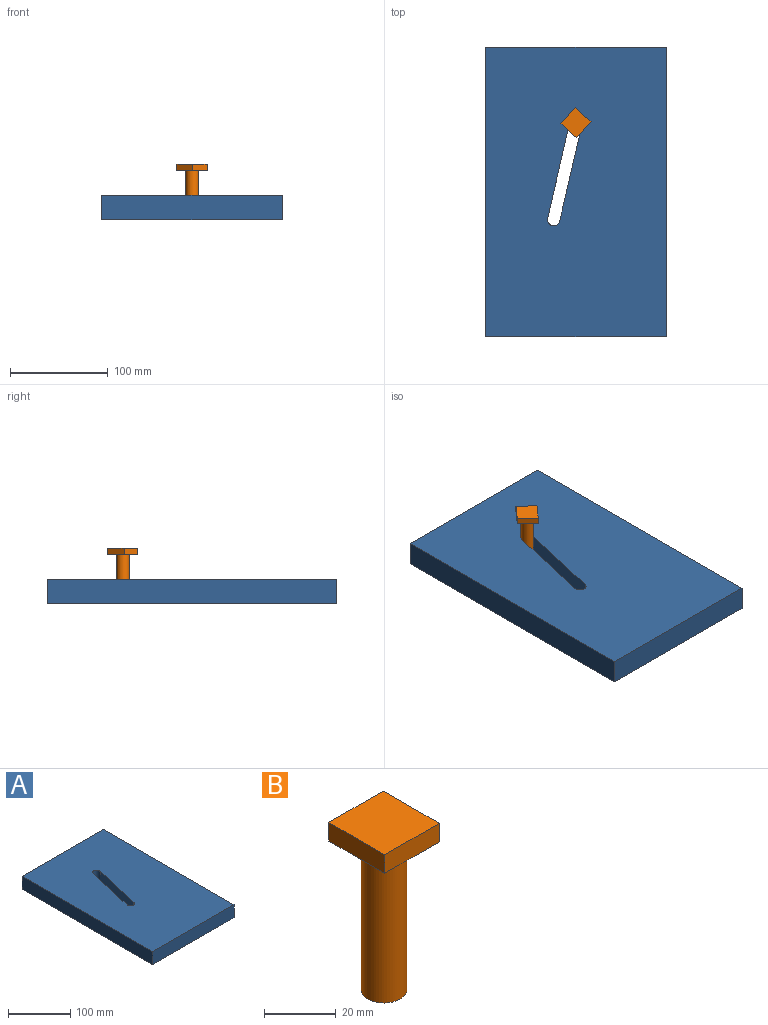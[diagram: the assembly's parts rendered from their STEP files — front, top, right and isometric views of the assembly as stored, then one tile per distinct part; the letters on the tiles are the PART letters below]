
ASSEMBLY  parts=2 mates=1
PART A: 10 faces, bbox 184.2x296x25.4 mm
  f0: plane 99.01x25.4mm, normal (-0.97,0.22,0), area 2580.6mm2, adj f1,f7,f8,f9
  f1: cylinder r=6.35mm len=25.4mm, axis (0,0,-1), area 506.7mm2, adj f0,f2,f8,f9
  f2: plane 99.01x25.4mm, normal (0.97,-0.22,0), area 2580.6mm2, adj f1,f7,f8,f9
  f3: plane 184.15x25.4mm, normal (0,1,0), area 4677.4mm2, adj f4,f6,f8,f9
  f4: plane 295.96x25.4mm, normal (-1,0,0), area 7517.4mm2, adj f3,f5,f8,f9
  f5: plane 184.15x25.4mm, normal (0,-1,0), area 4677.4mm2, adj f4,f6,f8,f9
  f6: plane 295.96x25.4mm, normal (1,0,0), area 7517.4mm2, adj f3,f5,f8,f9
  f7: cylinder r=6.35mm len=25.4mm, axis (0,0,-1), area 506.7mm2, adj f0,f2,f8,f9
  f8: plane 295.96x184.15mm, normal (0,0,1), area 53084.3mm2, adj f0,f1,f2,f3,f4,f5,f6,f7
  f9: plane 295.96x184.15mm, normal (0,0,-1), area 53084.3mm2, adj f0,f1,f2,f3,f4,f5,f6,f7
PART B: 8 faces, bbox 21.5x22.1x57.2 mm
  f0: cylinder r=6.35mm len=50.8mm, axis (0,0,-1), area 2026.8mm2, adj f1,f7
  f1: plane 12.7x12.7mm, normal (0,0,-1), area 126.7mm2, adj f0
  f2: plane 21.53x6.35mm, normal (0,1,0), area 136.7mm2, adj f3,f5,f6,f7
  f3: plane 22.12x6.35mm, normal (-1,0,0), area 140.4mm2, adj f2,f4,f6,f7
  f4: plane 21.53x6.35mm, normal (0,-1,0), area 136.7mm2, adj f3,f5,f6,f7
  f5: plane 22.12x6.35mm, normal (1,0,0), area 140.4mm2, adj f2,f4,f6,f7
  f6: plane 22.12x21.53mm, normal (0,0,1), area 476.1mm2, adj f2,f3,f4,f5
  f7: plane 22.12x21.53mm, normal (0,0,-1), area 349.4mm2, adj f0,f2,f3,f4,f5
PLACE A at identity fixed
PLACE B rot(axis=(0,0,-1),41.4deg) t=(-33.98,32.15,0)mm
MATE pin_slot B.f0 <-> A.f7  axis (0,0,-1) through (0,70.67,0)mm
